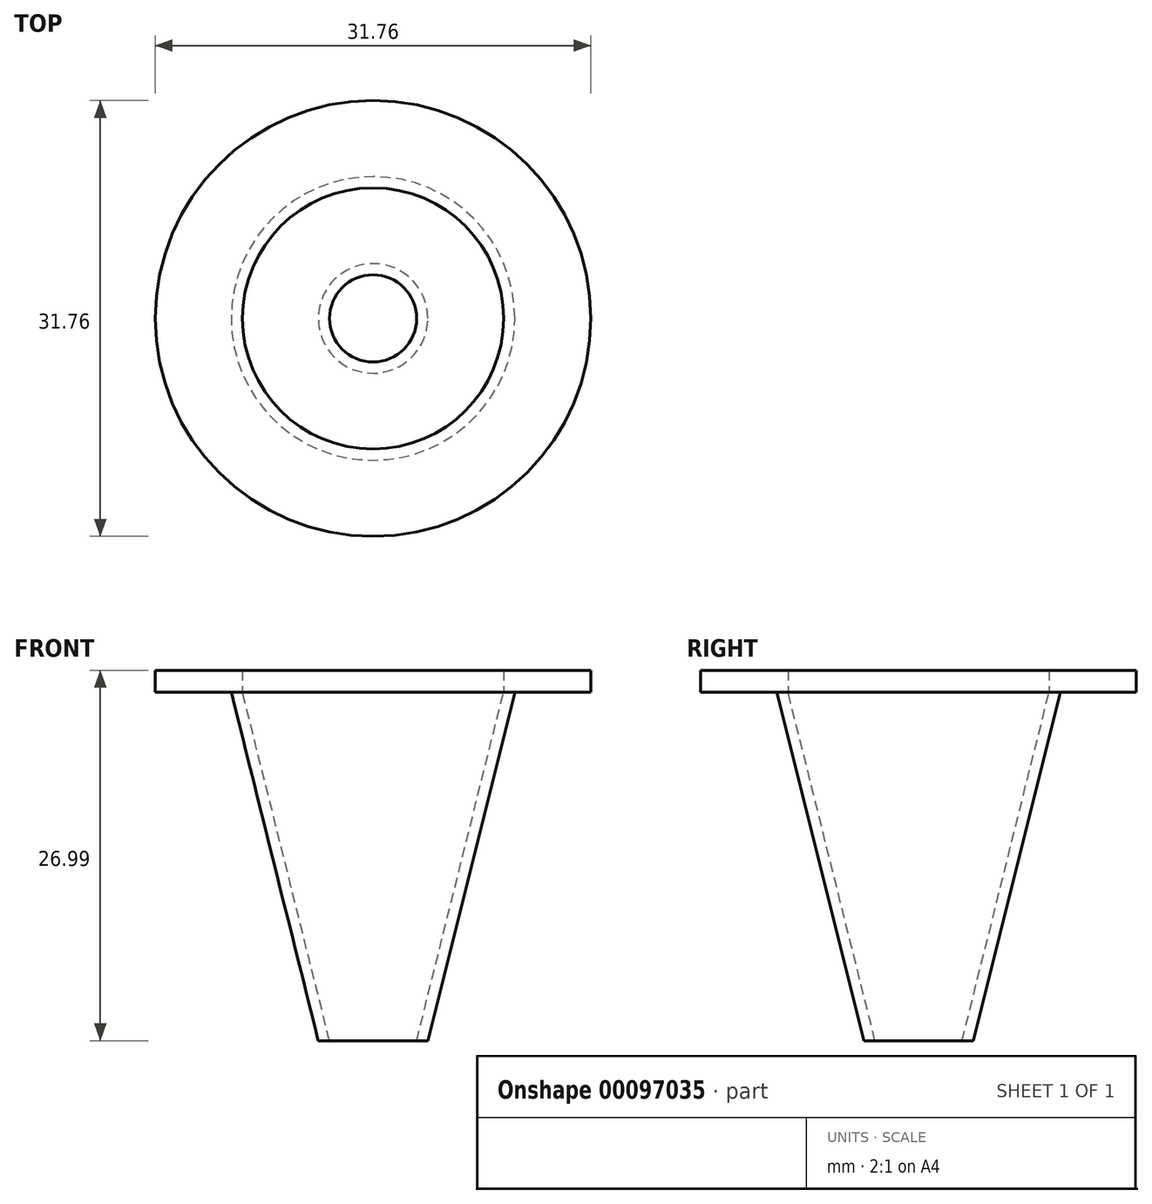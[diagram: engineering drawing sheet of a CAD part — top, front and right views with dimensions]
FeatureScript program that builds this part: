
annotation { "Feature Type Name" : "Feature", "Feature Type Description" : "" }
export const myFeature = defineFeature(function(context is Context, id is Id, definition is map)
    precondition{}
    {
        {
            var Q0;
            Q0=qCreatedBy(makeId("Front.planeOp"),FACE);
            var sketch = newSketch(context, id + "F0", { "sketchPlane" : qUnion([Q0])});
            skLineSegment(sketch, "E0", {"start": v(-9.51, 12.7) * mm, "end": v(-3.17, -12.7) * mm});
            skLineSegment(sketch, "E1", {"start": v(-4, -12.7) * mm, "end": v(-3.17, -12.7) * mm});
            skLineSegment(sketch, "E2.0", {"start": v(-10.33, 12.7) * mm, "end": v(-4, -12.7) * mm});
            skLineSegment(sketch, "E3", {"start": v(-10.33, 12.7) * mm, "end": v(-15.88, 12.7) * mm});
            skLineSegment(sketch, "E4", {"start": v(-15.88, 12.7) * mm, "end": v(-15.88, 14.29) * mm});
            skLineSegment(sketch, "E5", {"start": v(-15.88, 14.29) * mm, "end": v(-9.51, 14.29) * mm});
            skLineSegment(sketch, "E6", {"start": v(-9.51, 12.7) * mm, "end": v(-9.51, 14.29) * mm});
            skLineSegment(sketch, "E7", {"start": v(0, 0) * mm, "end": v(0, 10.04) * mm});
            skSolve(sketch);
        }
        {
            var Q0;
            Q0=makeQuery(id+"F0.imprint","IMPRINT",FACE,{"disambiguationData":[TD([[makeQuery(id+"F0.imprint","IMPRINT",EDGE,{"derivedFrom":sQuery(id+"F0.wireOp",EDGE,"E0")}),-1.0]])]});
            var Q1;
            Q1=sQuery(id+"F0.wireOp",EDGE,"E7");
            revolve(context, id + "F1", {"entities" : qUnion([Q0]), "axis" : qUnion([Q1]), "revolveType" : RevolveType.FULL});
        }
    });
